# Revit family: Chico-Ottoman_Chair-Via_Seating
name_source: partatom
category: Furniture
revit_build: Autodesk Revit 2014 (Build: 20130308_1515(x64)
units: mm (PartAtom-declared; Revit-internal decimal feet)

## types (2) — shared parameters
Aluminum = Aluminum
Assembly Code = E2020200
CYL = Steel, Chrome Plated
Fabric = Linen, White
HW = Aluminum
Keynote = 12500
Low Emitting Finish = Yes
Low Emitting Material = Yes
Manufacturer = VIA SEATING
Plastic = UHMW, Black
Salvage or Reuse = Yes
Type Comments = Ottoman
URL = www.viaseating.com
zero-valued in all types: Percentage of Recycled Content

## per-type parameters (varying)
| type | Description | Leg Type |
| 955-4POL | Fixed Height Swivel Base With Auto Return, 4 Leg Base | Otto 4 leg : 4POL |
| 955-DISC | Fixed Height Swivel Base With Auto Return, Disc Base | Otto Disc : DSC |

note: column(s) folded — value = type name in every type: Model

## geometry (parser evidence)
native form markers: Sweep x2
no freeform markers — native parametric forms only
